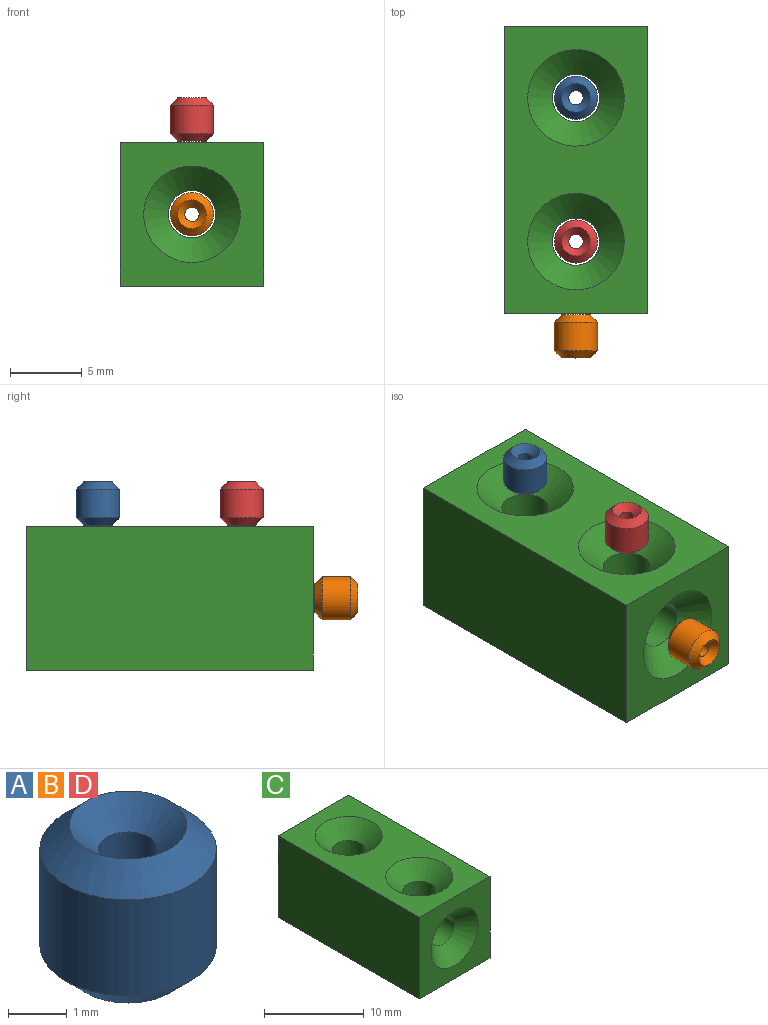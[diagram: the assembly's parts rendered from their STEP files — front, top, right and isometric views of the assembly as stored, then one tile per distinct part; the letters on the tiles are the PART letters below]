
ASSEMBLY  parts=4 mates=3
PART A: 6 faces, bbox 3x3x3 mm
  f0: cylinder r=0.5mm len=2mm, axis (0,0,-1), area 6.3mm2, adj f3,f4
  f1: cylinder r=1.5mm len=3mm, axis (0,0,-1), area 18.8mm2, adj f2,f5
  f2: cone r=1.5mm half-angle=45deg, axis (0,0,1), area 5.6mm2, adj f1,f3
  f3: cone r=1mm half-angle=45deg, axis (0,0,-1), area 3.3mm2, adj f0,f2
  f4: cone r=0.5mm half-angle=45deg, axis (0,0,1), area 3.3mm2, adj f0,f5
  f5: cone r=1mm half-angle=45deg, axis (0,0,-1), area 5.6mm2, adj f1,f4
PART B: same geometry as A
PART C: 16 faces, bbox 10x20x10 mm
  f0: cylinder r=1.65mm len=10mm, axis (0,-1,0), area 81.9mm2, adj f10,f12,f13,f14
  f1: cylinder r=1.65mm len=5mm, axis (0,-1,0), area 40.9mm2, adj f6,f13,f14
  f2: cylinder r=1.65mm len=3.3mm, axis (0,-1,0), area 23.2mm2, adj f9,f10,f12
  f3: plane 20x10mm, normal (-1,0,0), area 200mm2, adj f4,f6,f7,f8
  f4: plane 10x10mm, normal (0,-1,0), area 64.5mm2, adj f3,f5,f7,f8,f9
  f5: plane 20x10mm, normal (1,0,0), area 200mm2, adj f4,f6,f7,f8
  f6: plane 10x10mm, normal (0,1,0), area 91.4mm2, adj f1,f3,f5,f7,f8
  f7: plane 20x10mm, normal (0,0,1), area 129.1mm2, adj f3,f4,f5,f6,f11,f15
  f8: plane 20x10mm, normal (0,0,-1), area 182.9mm2, adj f3,f4,f5,f6,f12,f13
  f9: cone r=1.65mm half-angle=45deg, axis (0,-1,0), area 38.1mm2, adj f2,f4
  f10: cylinder r=1.65mm len=3.3mm, axis (0,0,1), area 23.2mm2, adj f0,f2,f11
  f11: cone r=1.65mm half-angle=45deg, axis (0,0,1), area 38.1mm2, adj f7,f10
  f12: cylinder r=1.65mm len=5mm, axis (0,0,1), area 40.9mm2, adj f0,f2,f8
  f13: cylinder r=1.65mm len=5mm, axis (0,0,1), area 40.9mm2, adj f0,f1,f8
  f14: cylinder r=1.65mm len=3.3mm, axis (0,0,1), area 23.2mm2, adj f0,f1,f15
  f15: cone r=1.65mm half-angle=45deg, axis (0,0,1), area 38.1mm2, adj f7,f14
PART D: same geometry as A
PLACE A t=(-7.66,10.29,-0.17)mm
PLACE B rot(axis=(1,0,0),90deg) t=(-7.66,-4.8,-5.26)mm
PLACE C t=(-22.23,11.27,-10.26)mm
PLACE D t=(-7.66,0.29,-0.17)mm
MATE slider C.f10 <-> D.f0  axis (0,0,1) through (-7.66,0.29,-0.26)mm
MATE slider C.f0 <-> B.f0  axis (0,-1,0) through (-7.66,-4.71,-5.26)mm
MATE slider C.f13 <-> A.f0  axis (0,0,1) through (-7.66,10.29,-0.26)mm
